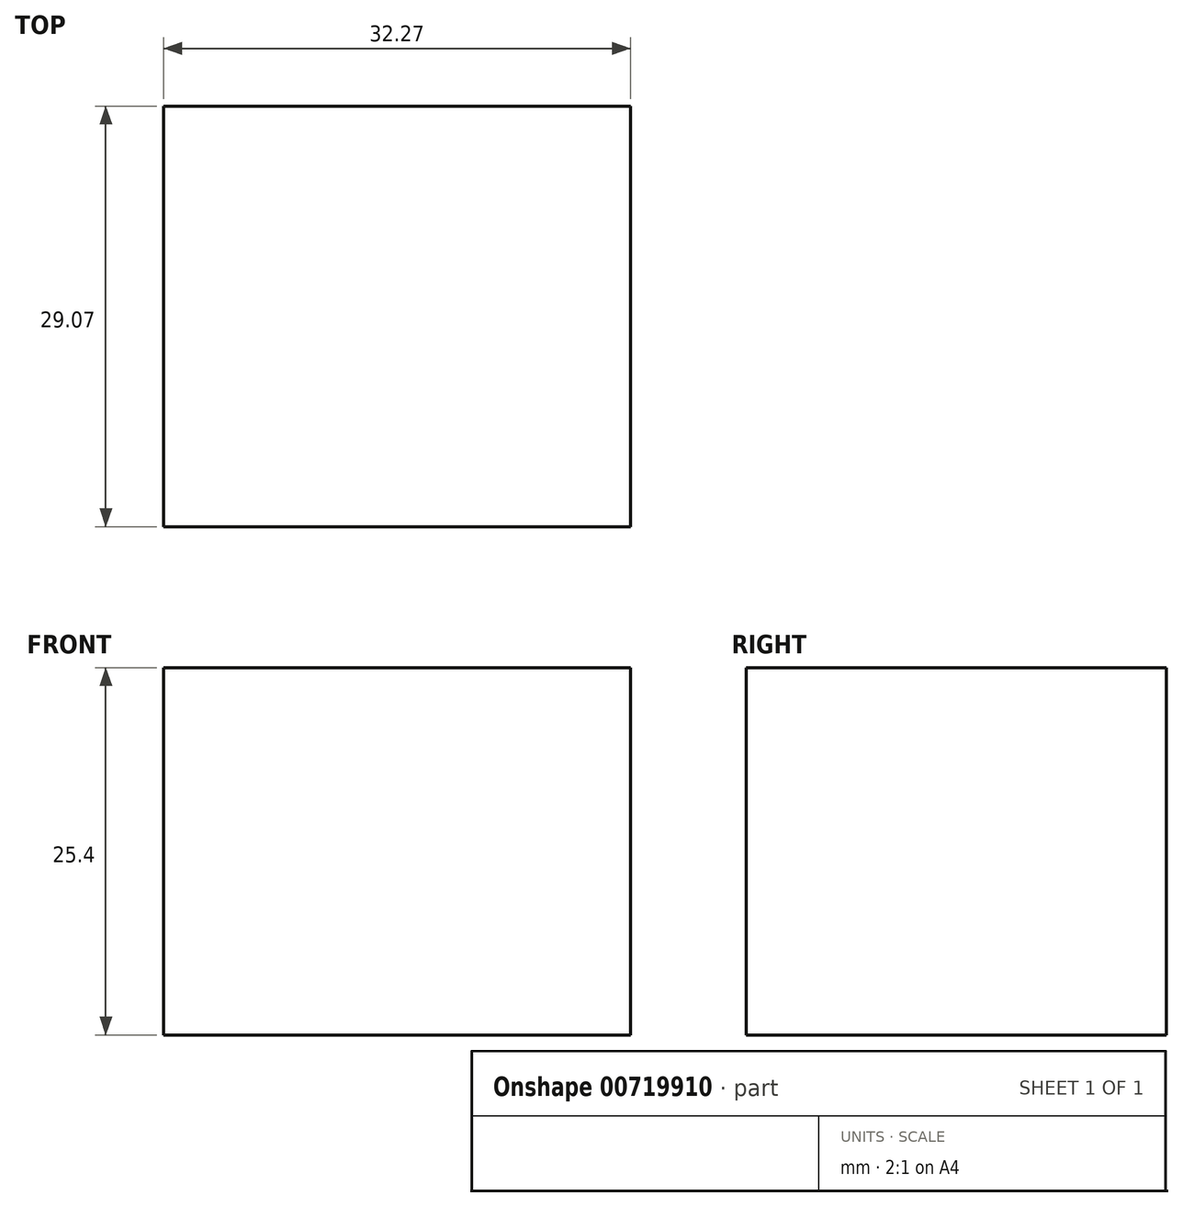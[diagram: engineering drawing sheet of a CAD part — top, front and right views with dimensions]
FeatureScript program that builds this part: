
annotation { "Feature Type Name" : "Feature", "Feature Type Description" : "" }
export const myFeature = defineFeature(function(context is Context, id is Id, definition is map)
    precondition{}
    {
        {
            var Q0;
            Q0=qCreatedBy(makeId("Top.planeOp"),FACE);
            var sketch = newSketch(context, id + "F0", { "sketchPlane" : qUnion([Q0])});
            skLineSegment(sketch, "E0.bottom", {"start": v(-53.28, -52.02) * mm, "end": v(-21, -52.02) * mm});
            skLineSegment(sketch, "E0.top", {"start": v(-53.28, -22.95) * mm, "end": v(-21, -22.95) * mm});
            skLineSegment(sketch, "E0.left", {"start": v(-53.28, -52.02) * mm, "end": v(-53.28, -22.95) * mm});
            skLineSegment(sketch, "E0.right", {"start": v(-21, -52.02) * mm, "end": v(-21, -22.95) * mm});
            skSolve(sketch);
        }
        {
            var Q0;
            Q0=makeQuery(id+"F0.imprint","IMPRINT",FACE,{"disambiguationData":[TD([[makeQuery(id+"F0.imprint","IMPRINT",EDGE,{"derivedFrom":sQuery(id+"F0.wireOp",EDGE,"E0.bottom")}),1.0]])]});
            extrude(context, id + "F1", {"entities" : qUnion([Q0]), "depth" : 25.4 * mm, "offsetDistance" : 25.4 * mm});
        }
    });
